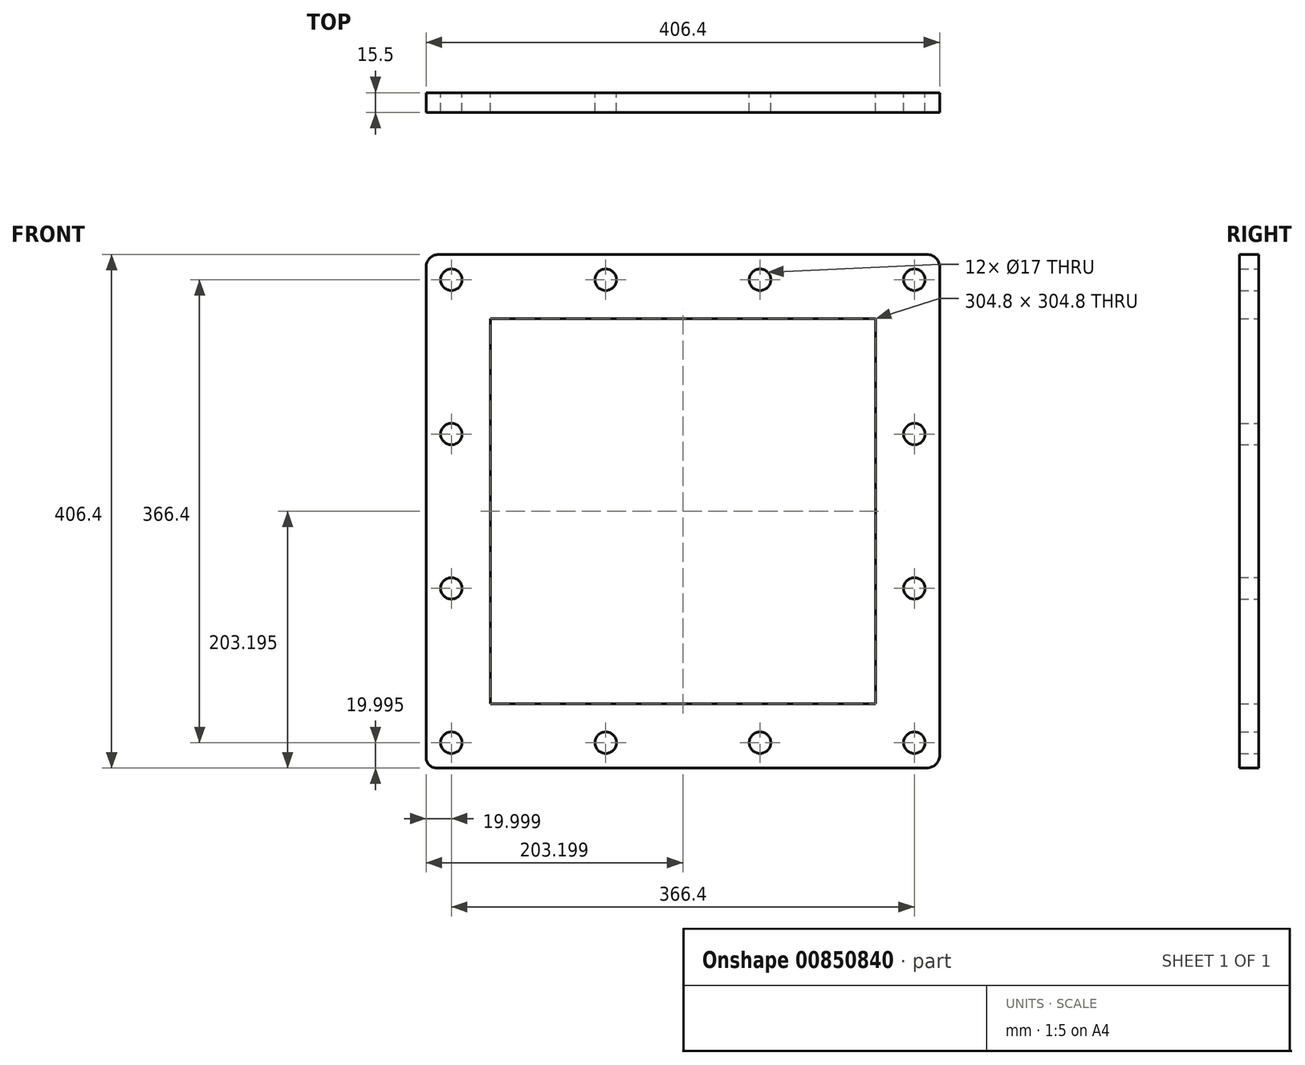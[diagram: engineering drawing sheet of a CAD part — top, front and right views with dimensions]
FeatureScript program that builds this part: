
annotation { "Feature Type Name" : "Feature", "Feature Type Description" : "" }
export const myFeature = defineFeature(function(context is Context, id is Id, definition is map)
    precondition{}
    {
        {
            var Q0;
            Q0=qCreatedBy(makeId("Front.planeOp"),FACE);
            var sketch = newSketch(context, id + "F0", { "sketchPlane" : qUnion([Q0])});
            skLineSegment(sketch, "E0", {"start": v(-316.68, 224.3) * mm, "end": v(-316.68, -163.9) * mm});
            skLineSegment(sketch, "E1", {"start": v(-308.49, -172.1) * mm, "end": v(79.72, -172.1) * mm});
            skLineSegment(sketch, "E2", {"start": v(89.72, -162.1) * mm, "end": v(89.72, 224.3) * mm});
            skLineSegment(sketch, "E3", {"start": v(79.72, 234.3) * mm, "end": v(-306.68, 234.3) * mm});
            skLineSegment(sketch, "E4.0", {"start": v(38.92, 183.5) * mm, "end": v(-265.88, 183.5) * mm});
            skLineSegment(sketch, "E5.0", {"start": v(38.92, -121.3) * mm, "end": v(38.92, 183.5) * mm});
            skLineSegment(sketch, "E6.0", {"start": v(-265.88, -121.3) * mm, "end": v(38.92, -121.3) * mm});
            skLineSegment(sketch, "E7.0", {"start": v(-265.88, 183.5) * mm, "end": v(-265.88, -121.3) * mm});
            skPoint(sketch, "E8.visualSharp", {"position": v(-316.68, 234.3) * mm});
            skArc(sketch, "E8.filletArc", {"start": v(-306.68, 234.3) * mm, "mid": v(-313.75, 231.38) * mm, "end": v(-316.68, 224.3) * mm});
            skPoint(sketch, "E9.visualSharp", {"position": v(89.72, 234.3) * mm});
            skArc(sketch, "E9.filletArc", {"start": v(89.72, 224.3) * mm, "mid": v(86.8, 231.38) * mm, "end": v(79.72, 234.3) * mm});
            skPoint(sketch, "E10.visualSharp", {"position": v(89.72, -172.1) * mm});
            skArc(sketch, "E10.filletArc", {"start": v(79.72, -172.1) * mm, "mid": v(86.8, -169.17) * mm, "end": v(89.72, -162.1) * mm});
            skPoint(sketch, "E11.visualSharp", {"position": v(-316.68, -172.1) * mm});
            skArc(sketch, "E11.filletArc", {"start": v(-316.68, -163.9) * mm, "mid": v(-314.28, -169.7) * mm, "end": v(-308.49, -172.1) * mm});
            skCircle(sketch, "E12", {"center": v(-296.68, 214.3) * mm, "radius": 8.5 * mm});
            skCircle(sketch, "E13", {"center": v(-174.55, 214.3) * mm, "radius": 8.5 * mm});
            skCircle(sketch, "E14", {"center": v(-52.41, 214.3) * mm, "radius": 8.5 * mm});
            skCircle(sketch, "E15", {"center": v(69.72, 214.3) * mm, "radius": 8.5 * mm});
            skCircle(sketch, "E16", {"center": v(69.72, 92.17) * mm, "radius": 8.5 * mm});
            skCircle(sketch, "E17", {"center": v(69.72, -29.96) * mm, "radius": 8.5 * mm});
            skCircle(sketch, "E18", {"center": v(69.72, -152.1) * mm, "radius": 8.5 * mm});
            skCircle(sketch, "E19", {"center": v(-52.41, -152.1) * mm, "radius": 8.5 * mm});
            skCircle(sketch, "E20", {"center": v(-174.55, -152.1) * mm, "radius": 8.5 * mm});
            skCircle(sketch, "E21", {"center": v(-296.68, -152.1) * mm, "radius": 8.5 * mm});
            skCircle(sketch, "E22", {"center": v(-296.68, -29.96) * mm, "radius": 8.5 * mm});
            skCircle(sketch, "E23", {"center": v(-296.68, 92.17) * mm, "radius": 8.5 * mm});
            skSolve(sketch);
        }
        {
            var Q0;
            Q0=makeQuery(id+"F0.imprint","IMPRINT",FACE,{"disambiguationData":[TD([[makeQuery(id+"F0.imprint","IMPRINT",EDGE,{"derivedFrom":sQuery(id+"F0.wireOp",EDGE,"E0")}),1.0]])]});
            extrude(context, id + "F1", {"entities" : qUnion([Q0]), "depth" : 15.5 * mm, "offsetDistance" : 25.4 * mm});
        }
    });
